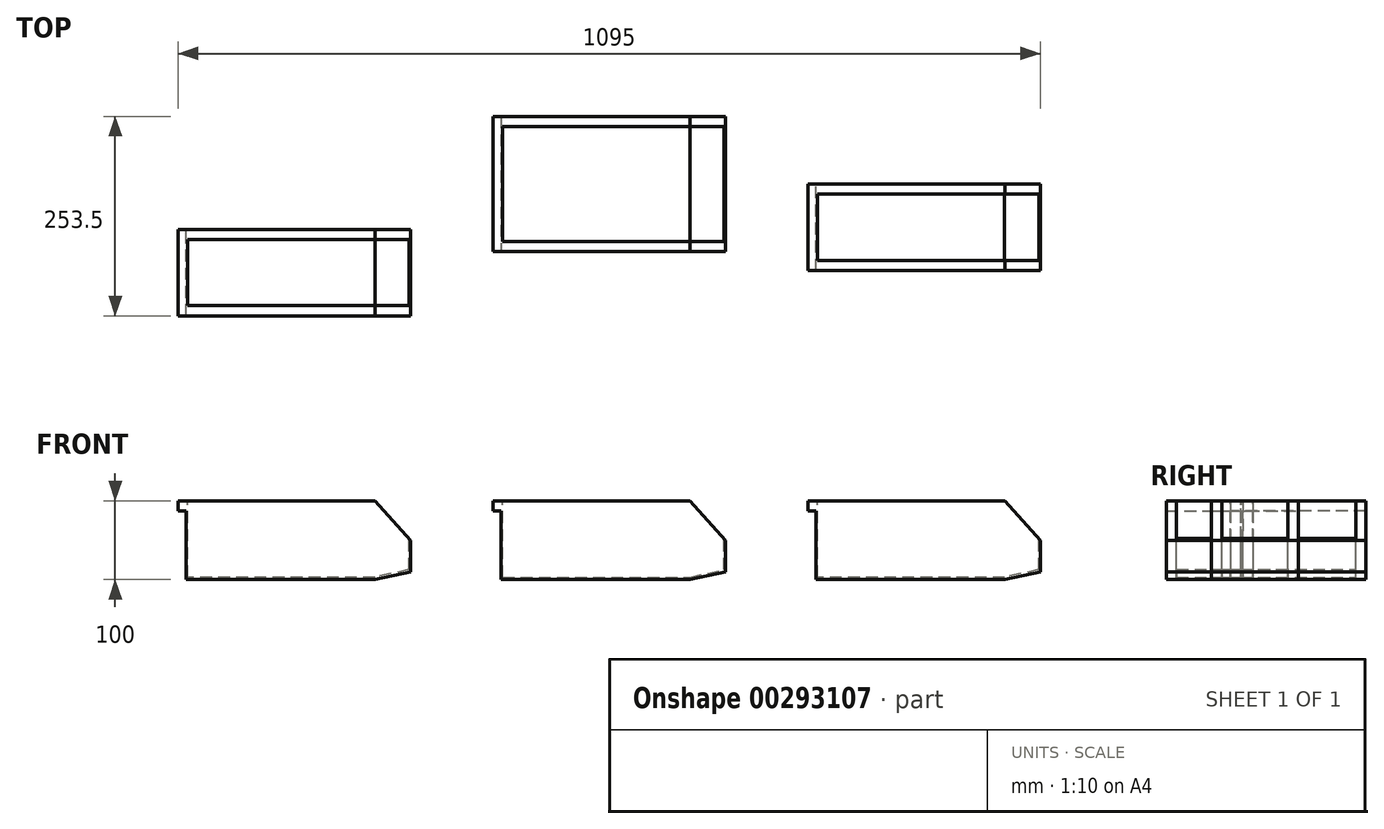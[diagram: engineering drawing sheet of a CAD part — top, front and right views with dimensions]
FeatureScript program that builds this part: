
annotation { "Feature Type Name" : "Feature", "Feature Type Description" : "" }
export const myFeature = defineFeature(function(context is Context, id is Id, definition is map)
    precondition{}
    {
        {
            var Q0;
            Q0=qCreatedBy(makeId("Top.planeOp"),FACE);
            var sketch = newSketch(context, id + "F0", { "sketchPlane" : qUnion([Q0])});
            skLineSegment(sketch, "E0.bottom", {"start": v(-147.5, 86) * mm, "end": v(147.5, 86) * mm});
            skLineSegment(sketch, "E0.top", {"start": v(-147.5, -86) * mm, "end": v(147.5, -86) * mm});
            skLineSegment(sketch, "E0.left", {"start": v(-147.5, 86) * mm, "end": v(-147.5, -86) * mm});
            skLineSegment(sketch, "E0.right", {"start": v(147.5, 86) * mm, "end": v(147.5, -86) * mm});
            skPoint(sketch, "E0.middle", {"position": v(0, 0) * mm});
            skSolve(sketch);
        }
        {
            var Q0;
            Q0=makeQuery(id+"F0.imprint","IMPRINT",FACE,{"disambiguationData":[TD([[makeQuery(id+"F0.imprint","IMPRINT",EDGE,{"derivedFrom":sQuery(id+"F0.wireOp",EDGE,"E0.bottom")}),-1.0]])]});
            extrude(context, id + "F1", {"entities" : qUnion([Q0]), "depth" : 100 * mm});
        }
        {
            var Q0;
            Q0=makeQuery(id+"F1.opExtrude","SWEPT_FACE",FACE,{"disambiguationData":[OSD([sQuery(id+"F0.wireOp",EDGE,"E0.top")])]});
            var sketch = newSketch(context, id + "F2", { "sketchPlane" : qUnion([Q0])});
            skLineSegment(sketch, "E1", {"start": v(147.5, 10) * mm, "end": v(147.5, 50) * mm});
            skLineSegment(sketch, "E2", {"start": v(147.5, 50) * mm, "end": v(102.5, 100) * mm});
            skLineSegment(sketch, "E3", {"start": v(102.5, 100) * mm, "end": v(-147.5, 100) * mm});
            skLineSegment(sketch, "E4", {"start": v(-147.5, 100) * mm, "end": v(-147.5, 87) * mm});
            skLineSegment(sketch, "E5", {"start": v(-147.5, 87) * mm, "end": v(-137.5, 87) * mm});
            skLineSegment(sketch, "E6", {"start": v(-137.5, 87) * mm, "end": v(-137.5, 0) * mm});
            skLineSegment(sketch, "E7", {"start": v(-137.5, 0) * mm, "end": v(102.5, 0) * mm});
            skLineSegment(sketch, "E8", {"start": v(102.5, 0) * mm, "end": v(147.5, 10) * mm});
            skPoint(sketch, "E9", {"position": v(102.5, 0) * mm});
            skSolve(sketch);
        }
        {
            var Q0;
            Q0=makeQuery(id+"F1.opExtrude","CAP_FACE",FACE,{"disambiguationData":[OSD([sQuery(id+"F0.wireOp",EDGE,"E0.bottom"),sQuery(id+"F0.wireOp",EDGE,"E0.top"),sQuery(id+"F0.wireOp",EDGE,"E0.left"),sQuery(id+"F0.wireOp",EDGE,"E0.right")])],"isStart":false});
            var sketch = newSketch(context, id + "F3", { "sketchPlane" : qUnion([Q0])});
            skLineSegment(sketch, "E10.bottom", {"start": v(-135.5, -73) * mm, "end": v(145.5, -73) * mm});
            skLineSegment(sketch, "E10.top", {"start": v(-135.5, 73) * mm, "end": v(145.5, 73) * mm});
            skLineSegment(sketch, "E10.left", {"start": v(-135.5, -73) * mm, "end": v(-135.5, 73) * mm});
            skLineSegment(sketch, "E10.right", {"start": v(145.5, -73) * mm, "end": v(145.5, 73) * mm});
            skSolve(sketch);
        }
        {
            var Q0;
            Q0=makeQuery(id+"F3.imprint","IMPRINT",FACE,{"disambiguationData":[TD([[makeQuery(id+"F3.imprint","IMPRINT",EDGE,{"derivedFrom":sQuery(id+"F3.wireOp",EDGE,"E10.bottom")}),1.0]])]});
            extrude(context, id + "F4", {"entities" : qUnion([Q0]), "operationType" : NewBodyOperationType.REMOVE, "oppositeDirection" : true, "depth" : 97 * mm});
        }
        {
            var Q0;
            {var subQ0=sQuery(id+"F2.wireOp",EDGE,"E5");Q0=makeQuery(id+"F2.imprint","IMPRINT",FACE,{"disambiguationData":[TD([[makeQuery(id+"F2.imprint","IMPRINT",EDGE,{"derivedFrom":subQ0}),-1.0]])]});}
            var Q1;
            {var subQ0=sQuery(id+"F2.wireOp",EDGE,"E2");Q1=makeQuery(id+"F2.imprint","IMPRINT",FACE,{"disambiguationData":[TD([[makeQuery(id+"F2.imprint","IMPRINT",EDGE,{"derivedFrom":subQ0}),-1.0]])]});}
            var Q2;
            {var subQ0=sQuery(id+"F2.wireOp",EDGE,"E8");Q2=makeQuery(id+"F2.imprint","IMPRINT",FACE,{"disambiguationData":[TD([[makeQuery(id+"F2.imprint","IMPRINT",EDGE,{"derivedFrom":subQ0}),-1.0]])]});}
            extrude(context, id + "F5", {"entities" : qUnion([Q0, Q1, Q2]), "operationType" : NewBodyOperationType.REMOVE, "endBound" : BoundingType.THROUGH_ALL, "oppositeDirection" : true, "depth" : 25 * mm});
        }
        {
            var Q0;
            Q0=makeQuery(id+"F5.boolean.opBoolean","COPY",FACE,{"derivedFrom":makeQuery(id+"F5.opExtrude","SWEPT_FACE",FACE,{"disambiguationData":[OSD([sQuery(id+"F2.wireOp",EDGE,"E8")])]})});
            var sketch = newSketch(context, id + "F6", { "sketchPlane" : qUnion([Q0])});
            skLineSegment(sketch, "E11.bottom", {"start": v(100.06, -86) * mm, "end": v(146.16, -86) * mm});
            skLineSegment(sketch, "E11.top", {"start": v(100.06, 86) * mm, "end": v(146.16, 86) * mm});
            skLineSegment(sketch, "E11.left", {"start": v(100.06, -86) * mm, "end": v(100.06, 86) * mm});
            skLineSegment(sketch, "E11.right", {"start": v(146.16, -86) * mm, "end": v(146.16, 86) * mm});
            skSolve(sketch);
        }
        {
            var Q0;
            Q0=makeQuery(id+"F6.imprint","IMPRINT",FACE,{"disambiguationData":[TD([[makeQuery(id+"F6.imprint","IMPRINT",EDGE,{"derivedFrom":sQuery(id+"F6.wireOp",EDGE,"E11.bottom")}),-1.0]])]});
            var Q1;
            {var subQ0=makeQuery(id+"F5.opExtrude","SWEPT_FACE",FACE,{"disambiguationData":[OSD([sQuery(id+"F2.wireOp",EDGE,"E8")])]});var subQ1=sQuery(id+"F3.wireOp",EDGE,"E10.bottom");Q1=makeQuery(id+"F6.imprint","IMPRINT",FACE,{"disambiguationData":[TD([[makeQuery(id+"F6.imprint","IMPRINT",EDGE,{"derivedFrom":makeQuery(id+"F5.boolean.opBoolean","INTERSECT",EDGE,{"derivedFrom":[makeQuery(id+"F4.boolean.opBoolean","COPY",FACE,{"derivedFrom":makeQuery(id+"F4.opExtrude","SWEPT_FACE",FACE,{"disambiguationData":[OSD([subQ1])]})}),subQ0]})}),-1.0]])]});}
            extrude(context, id + "F7", {"entities" : qUnion([Q0, Q1]), "operationType" : NewBodyOperationType.ADD, "oppositeDirection" : true, "depth" : 3 * mm});
        }
        {
            var Q0;
            Q0=qCreatedBy(makeId("Top.planeOp"),FACE);
            var sketch = newSketch(context, id + "F8", { "sketchPlane" : qUnion([Q0])});
            skLineSegment(sketch, "E12.bottom", {"start": v(252.5, 0) * mm, "end": v(547.5, 0) * mm});
            skLineSegment(sketch, "E12.top", {"start": v(252.5, -110) * mm, "end": v(547.5, -110) * mm});
            skLineSegment(sketch, "E12.left", {"start": v(252.5, 0) * mm, "end": v(252.5, -110) * mm});
            skLineSegment(sketch, "E12.right", {"start": v(547.5, 0) * mm, "end": v(547.5, -110) * mm});
            skPoint(sketch, "E12.middle", {"position": v(400, -55) * mm});
            skLineSegment(sketch, "E13.bottom", {"start": v(-547.5, -57.5) * mm, "end": v(-252.5, -57.5) * mm});
            skLineSegment(sketch, "E13.top", {"start": v(-547.5, -167.5) * mm, "end": v(-252.5, -167.5) * mm});
            skLineSegment(sketch, "E13.left", {"start": v(-547.5, -57.5) * mm, "end": v(-547.5, -167.5) * mm});
            skLineSegment(sketch, "E13.right", {"start": v(-252.5, -57.5) * mm, "end": v(-252.5, -167.5) * mm});
            skPoint(sketch, "E13.middle", {"position": v(-400, -112.5) * mm});
            skSolve(sketch);
        }
        {
            var Q0;
            Q0=makeQuery(id+"F8.imprint","IMPRINT",FACE,{"disambiguationData":[TD([[makeQuery(id+"F8.imprint","IMPRINT",EDGE,{"derivedFrom":sQuery(id+"F8.wireOp",EDGE,"E12.bottom")}),-1.0]])]});
            var Q1;
            Q1=makeQuery(id+"F8.imprint","IMPRINT",FACE,{"disambiguationData":[TD([[makeQuery(id+"F8.imprint","IMPRINT",EDGE,{"derivedFrom":sQuery(id+"F8.wireOp",EDGE,"E13.bottom")}),-1.0]])]});
            extrude(context, id + "F9", {"entities" : qUnion([Q0, Q1]), "depth" : 100 * mm});
        }
        {
            var Q0;
            Q0=makeQuery(id+"F9.opExtrude","SWEPT_FACE",FACE,{"disambiguationData":[OSD([sQuery(id+"F8.wireOp",EDGE,"E12.bottom")])]});
            var sketch = newSketch(context, id + "F10", { "sketchPlane" : qUnion([Q0])});
            skLineSegment(sketch, "E14", {"start": v(-547.5, 10) * mm, "end": v(-547.5, 50) * mm});
            skLineSegment(sketch, "E15", {"start": v(-547.5, 50) * mm, "end": v(-502.5, 100) * mm});
            skLineSegment(sketch, "E16", {"start": v(-502.5, 100) * mm, "end": v(-252.5, 100) * mm});
            skLineSegment(sketch, "E17", {"start": v(-252.5, 100) * mm, "end": v(-252.5, 87) * mm});
            skLineSegment(sketch, "E18", {"start": v(-252.5, 87) * mm, "end": v(-262.5, 87) * mm});
            skLineSegment(sketch, "E19", {"start": v(-262.5, 87) * mm, "end": v(-262.5, 0) * mm});
            skLineSegment(sketch, "E20", {"start": v(-262.5, 0) * mm, "end": v(-502.5, 0) * mm});
            skLineSegment(sketch, "E21", {"start": v(-502.5, 0) * mm, "end": v(-547.5, 10) * mm});
            skPoint(sketch, "E22", {"position": v(-502.5, 0) * mm});
            skSolve(sketch);
        }
        {
            var Q0;
            Q0=makeQuery(id+"F9.opExtrude","SWEPT_FACE",FACE,{"disambiguationData":[OSD([sQuery(id+"F8.wireOp",EDGE,"E13.bottom")])]});
            var sketch = newSketch(context, id + "F11", { "sketchPlane" : qUnion([Q0])});
            skLineSegment(sketch, "E23", {"start": v(297.5, 100) * mm, "end": v(547.5, 100) * mm});
            skLineSegment(sketch, "E24", {"start": v(547.5, 100) * mm, "end": v(547.5, 87) * mm});
            skLineSegment(sketch, "E25", {"start": v(547.5, 87) * mm, "end": v(537.5, 87) * mm});
            skLineSegment(sketch, "E26", {"start": v(537.5, 87) * mm, "end": v(537.5, 0) * mm});
            skLineSegment(sketch, "E27", {"start": v(537.5, 0) * mm, "end": v(297.5, 0) * mm});
            skLineSegment(sketch, "E28", {"start": v(297.5, 0) * mm, "end": v(252.5, 10) * mm});
            skLineSegment(sketch, "E29", {"start": v(252.5, 10) * mm, "end": v(252.5, 50) * mm});
            skLineSegment(sketch, "E30", {"start": v(252.5, 50) * mm, "end": v(297.5, 100) * mm});
            skSolve(sketch);
        }
        {
            var Q0;
            Q0=makeQuery(id+"F9.opExtrude","CAP_FACE",FACE,{"disambiguationData":[OSD([sQuery(id+"F8.wireOp",EDGE,"E12.bottom"),sQuery(id+"F8.wireOp",EDGE,"E12.top"),sQuery(id+"F8.wireOp",EDGE,"E12.left"),sQuery(id+"F8.wireOp",EDGE,"E12.right")])],"isStart":false});
            var sketch = newSketch(context, id + "F12", { "sketchPlane" : qUnion([Q0])});
            skLineSegment(sketch, "E31.bottom", {"start": v(545.5, -97) * mm, "end": v(264.5, -97) * mm});
            skLineSegment(sketch, "E31.top", {"start": v(545.5, -13) * mm, "end": v(264.5, -13) * mm});
            skLineSegment(sketch, "E31.left", {"start": v(545.5, -97) * mm, "end": v(545.5, -13) * mm});
            skLineSegment(sketch, "E31.right", {"start": v(264.5, -97) * mm, "end": v(264.5, -13) * mm});
            skLineSegment(sketch, "E32.bottom", {"start": v(-254.5, -154.5) * mm, "end": v(-535.5, -154.5) * mm});
            skLineSegment(sketch, "E32.top", {"start": v(-254.5, -70.5) * mm, "end": v(-535.5, -70.5) * mm});
            skLineSegment(sketch, "E32.left", {"start": v(-254.5, -154.5) * mm, "end": v(-254.5, -70.5) * mm});
            skLineSegment(sketch, "E32.right", {"start": v(-535.5, -154.5) * mm, "end": v(-535.5, -70.5) * mm});
            skSolve(sketch);
        }
        {
            var Q0;
            Q0=makeQuery(id+"F12.imprint","IMPRINT",FACE,{"disambiguationData":[TD([[makeQuery(id+"F12.imprint","IMPRINT",EDGE,{"derivedFrom":sQuery(id+"F12.wireOp",EDGE,"E31.bottom")}),-1.0]])]});
            extrude(context, id + "F13", {"entities" : qUnion([Q0]), "operationType" : NewBodyOperationType.REMOVE, "oppositeDirection" : true, "depth" : 97 * mm});
        }
        {
            var Q0;
            {var subQ0=sQuery(id+"F10.wireOp",EDGE,"E15");Q0=makeQuery(id+"F10.imprint","IMPRINT",FACE,{"disambiguationData":[TD([[makeQuery(id+"F10.imprint","IMPRINT",EDGE,{"derivedFrom":subQ0}),1.0]])]});}
            var Q1;
            {var subQ0=sQuery(id+"F10.wireOp",EDGE,"E21");Q1=makeQuery(id+"F10.imprint","IMPRINT",FACE,{"disambiguationData":[TD([[makeQuery(id+"F10.imprint","IMPRINT",EDGE,{"derivedFrom":subQ0}),1.0]])]});}
            var Q2;
            {var subQ0=sQuery(id+"F10.wireOp",EDGE,"E18");Q2=makeQuery(id+"F10.imprint","IMPRINT",FACE,{"disambiguationData":[TD([[makeQuery(id+"F10.imprint","IMPRINT",EDGE,{"derivedFrom":subQ0}),1.0]])]});}
            extrude(context, id + "F14", {"entities" : qUnion([Q0, Q1, Q2]), "operationType" : NewBodyOperationType.REMOVE, "endBound" : BoundingType.THROUGH_ALL, "oppositeDirection" : true, "depth" : 25 * mm});
        }
        {
            var Q0;
            {var subQ0=sQuery(id+"F11.wireOp",EDGE,"E30");Q0=makeQuery(id+"F11.imprint","IMPRINT",FACE,{"disambiguationData":[TD([[makeQuery(id+"F11.imprint","IMPRINT",EDGE,{"derivedFrom":subQ0}),1.0]])]});}
            var Q1;
            {var subQ0=sQuery(id+"F11.wireOp",EDGE,"E28");Q1=makeQuery(id+"F11.imprint","IMPRINT",FACE,{"disambiguationData":[TD([[makeQuery(id+"F11.imprint","IMPRINT",EDGE,{"derivedFrom":subQ0}),1.0]])]});}
            var Q2;
            {var subQ0=sQuery(id+"F11.wireOp",EDGE,"E25");Q2=makeQuery(id+"F11.imprint","IMPRINT",FACE,{"disambiguationData":[TD([[makeQuery(id+"F11.imprint","IMPRINT",EDGE,{"derivedFrom":subQ0}),1.0]])]});}
            extrude(context, id + "F15", {"entities" : qUnion([Q0, Q1, Q2]), "operationType" : NewBodyOperationType.REMOVE, "endBound" : BoundingType.THROUGH_ALL, "oppositeDirection" : true, "depth" : 25 * mm});
        }
        {
            var Q0;
            Q0=makeQuery(id+"F12.imprint","IMPRINT",FACE,{"disambiguationData":[TD([[makeQuery(id+"F12.imprint","IMPRINT",EDGE,{"derivedFrom":sQuery(id+"F12.wireOp",EDGE,"E32.bottom")}),-1.0]])]});
            extrude(context, id + "F16", {"entities" : qUnion([Q0]), "operationType" : NewBodyOperationType.REMOVE, "oppositeDirection" : true, "depth" : 97 * mm});
        }
        {
            var Q0;
            Q0=makeQuery(id+"F14.boolean.opBoolean","COPY",FACE,{"derivedFrom":makeQuery(id+"F14.opExtrude","SWEPT_FACE",FACE,{"disambiguationData":[OSD([sQuery(id+"F10.wireOp",EDGE,"E21")])]})});
            var sketch = newSketch(context, id + "F17", { "sketchPlane" : qUnion([Q0])});
            skLineSegment(sketch, "E33.bottom", {"start": v(490.53, 110) * mm, "end": v(536.63, 110) * mm});
            skLineSegment(sketch, "E33.top", {"start": v(490.53, 0) * mm, "end": v(536.63, 0) * mm});
            skLineSegment(sketch, "E33.left", {"start": v(536.63, 110) * mm, "end": v(536.63, 0) * mm});
            skLineSegment(sketch, "E33.right", {"start": v(490.53, 110) * mm, "end": v(490.53, 0) * mm});
            skSolve(sketch);
        }
        {
            var Q0;
            Q0=makeQuery(id+"F17.imprint","IMPRINT",FACE,{"disambiguationData":[TD([[makeQuery(id+"F17.imprint","IMPRINT",EDGE,{"derivedFrom":sQuery(id+"F17.wireOp",EDGE,"E33.bottom")}),-1.0]])]});
            var Q1;
            {var subQ0=makeQuery(id+"F14.opExtrude","SWEPT_FACE",FACE,{"disambiguationData":[OSD([sQuery(id+"F10.wireOp",EDGE,"E21")])]});var subQ1=sQuery(id+"F12.wireOp",EDGE,"E31.bottom");Q1=makeQuery(id+"F17.imprint","IMPRINT",FACE,{"disambiguationData":[TD([[makeQuery(id+"F17.imprint","IMPRINT",EDGE,{"derivedFrom":makeQuery(id+"F14.boolean.opBoolean","INTERSECT",EDGE,{"derivedFrom":[makeQuery(id+"F13.boolean.opBoolean","COPY",FACE,{"derivedFrom":makeQuery(id+"F13.opExtrude","SWEPT_FACE",FACE,{"disambiguationData":[OSD([subQ1])]})}),subQ0]})}),-1.0]])]});}
            extrude(context, id + "F18", {"entities" : qUnion([Q0, Q1]), "operationType" : NewBodyOperationType.ADD, "oppositeDirection" : true, "depth" : 3 * mm});
        }
        {
            var Q0;
            Q0=makeQuery(id+"F15.boolean.opBoolean","COPY",FACE,{"derivedFrom":makeQuery(id+"F15.opExtrude","SWEPT_FACE",FACE,{"disambiguationData":[OSD([sQuery(id+"F11.wireOp",EDGE,"E28")])]})});
            var sketch = newSketch(context, id + "F19", { "sketchPlane" : qUnion([Q0])});
            skLineSegment(sketch, "E34.bottom", {"start": v(-290.42, 167.5) * mm, "end": v(-244.32, 167.5) * mm});
            skLineSegment(sketch, "E34.top", {"start": v(-290.42, 57.5) * mm, "end": v(-244.32, 57.5) * mm});
            skLineSegment(sketch, "E34.left", {"start": v(-244.32, 167.5) * mm, "end": v(-244.32, 57.5) * mm});
            skLineSegment(sketch, "E34.right", {"start": v(-290.42, 167.5) * mm, "end": v(-290.42, 57.5) * mm});
            skSolve(sketch);
        }
        {
            var Q0;
            Q0=makeQuery(id+"F19.imprint","IMPRINT",FACE,{"disambiguationData":[TD([[makeQuery(id+"F19.imprint","IMPRINT",EDGE,{"derivedFrom":sQuery(id+"F19.wireOp",EDGE,"E34.bottom")}),-1.0]])]});
            var Q1;
            {var subQ0=sQuery(id+"F12.wireOp",EDGE,"E32.bottom");var subQ1=makeQuery(id+"F15.boolean.opBoolean","COPY",FACE,{"derivedFrom":makeQuery(id+"F15.opExtrude","SWEPT_FACE",FACE,{"disambiguationData":[OSD([sQuery(id+"F11.wireOp",EDGE,"E28")])]})});Q1=makeQuery(id+"F19.imprint","IMPRINT",FACE,{"disambiguationData":[TD([[makeQuery(id+"F19.imprint","IMPRINT",EDGE,{"derivedFrom":makeQuery(id+"F16.boolean.opBoolean","INTERSECT",EDGE,{"derivedFrom":[subQ1,makeQuery(id+"F16.opExtrude","SWEPT_FACE",FACE,{"disambiguationData":[OSD([subQ0])]})]})}),1.0]])]});}
            extrude(context, id + "F20", {"entities" : qUnion([Q0, Q1]), "operationType" : NewBodyOperationType.ADD, "oppositeDirection" : true, "depth" : 3 * mm});
        }
    });
